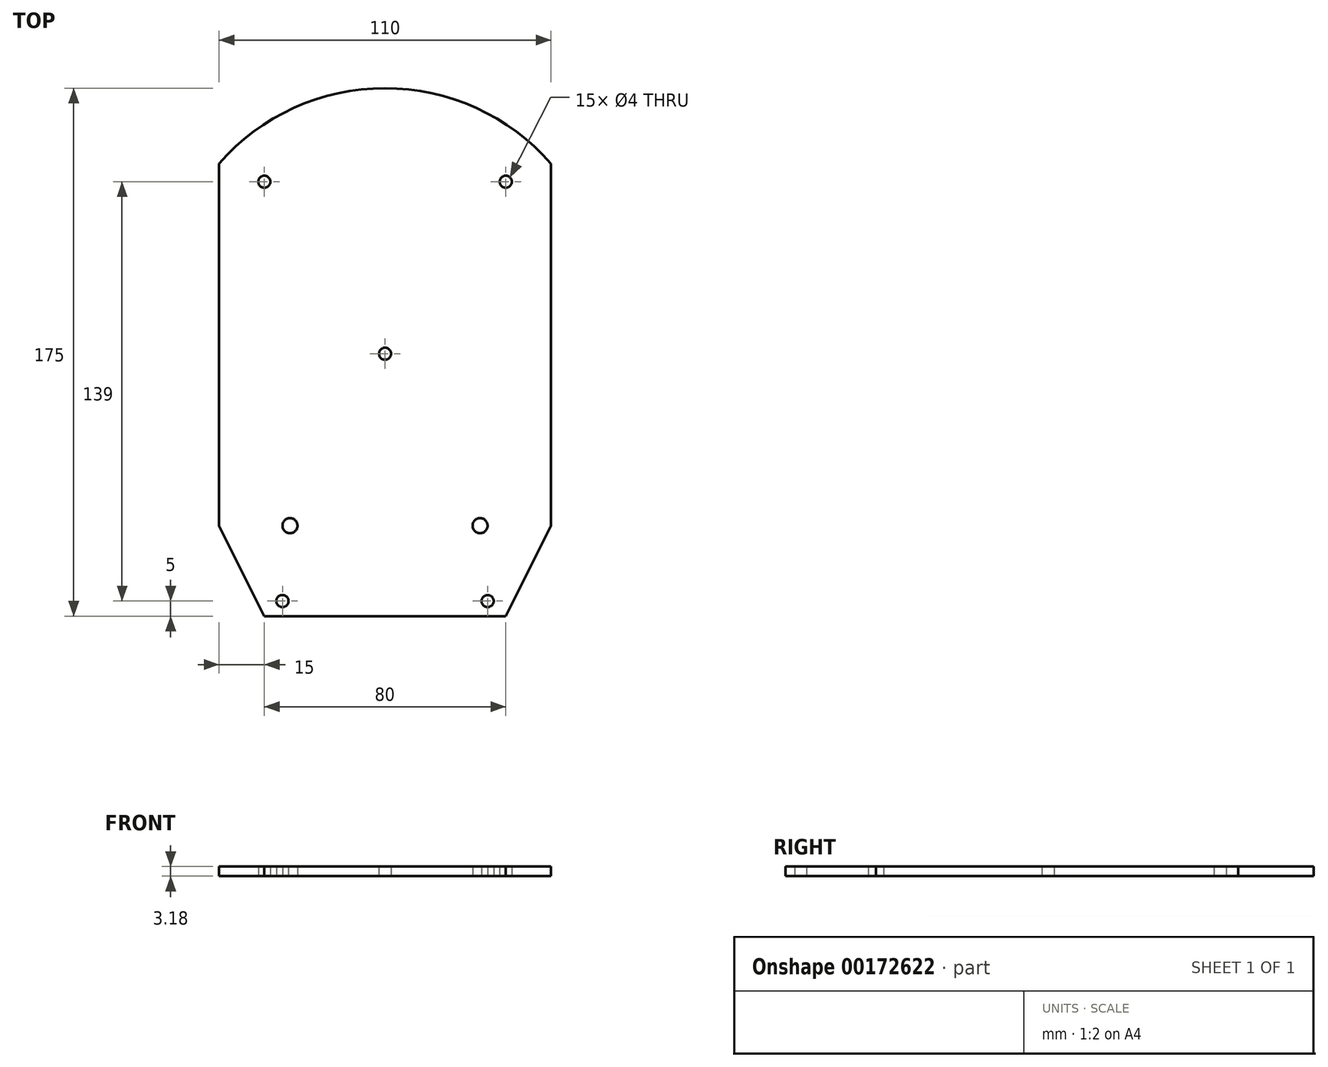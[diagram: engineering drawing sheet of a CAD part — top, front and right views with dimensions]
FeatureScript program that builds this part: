
annotation { "Feature Type Name" : "Feature", "Feature Type Description" : "" }
export const myFeature = defineFeature(function(context is Context, id is Id, definition is map)
    precondition{}
    {
        {
            var Q0;
            Q0=qCreatedBy(makeId("Top.planeOp"),FACE);
            var sketch = newSketch(context, id + "F0", { "sketchPlane" : qUnion([Q0])});
            skLineSegment(sketch, "E0.top", {"start": v(-40, -87.5) * mm, "end": v(40, -87.5) * mm});
            skLineSegment(sketch, "E0.left", {"start": v(-55, 62.5) * mm, "end": v(-55, -57.5) * mm});
            skLineSegment(sketch, "E0.right", {"start": v(55, 62.5) * mm, "end": v(55, -57.5) * mm});
            skPoint(sketch, "E0.middle", {"position": v(0, 0) * mm});
            skPoint(sketch, "E1", {"position": v(0, -87.5) * mm});
            skPoint(sketch, "E2", {"position": v(-40, -87.5) * mm});
            skPoint(sketch, "E3", {"position": v(40, -87.5) * mm});
            skLineSegment(sketch, "E4", {"start": v(-55, -57.5) * mm, "end": v(-40, -87.5) * mm});
            skLineSegment(sketch, "E5", {"start": v(55, -57.5) * mm, "end": v(40, -87.5) * mm});
            skPoint(sketch, "E6", {"position": v(0, 87.5) * mm});
            skArc(sketch, "E7", {"start": v(55, 62.5) * mm, "mid": v(0, 87.5) * mm, "end": v(-55, 62.5) * mm});
            skPoint(sketch, "E8", {"position": v(-34, -82.5) * mm});
            skCircle(sketch, "E9", {"center": v(-34, -82.5) * mm, "radius": 2 * mm});
            skPoint(sketch, "E10", {"position": v(-40, 56.5) * mm});
            skLineSegment(sketch, "E11", {"start": v(-55, 62.5) * mm, "end": v(-16.67, 62.5) * mm, "construction": true});
            skCircle(sketch, "E12", {"center": v(-40, 56.5) * mm, "radius": 2 * mm});
            skCircle(sketch, "E13.MirrorC", {"center": v(40, 56.5) * mm, "radius": 2 * mm});
            skCircle(sketch, "E14.MirrorC", {"center": v(34, -82.5) * mm, "radius": 2 * mm});
            skPoint(sketch, "E15", {"position": v(0, -0.5) * mm});
            skCircle(sketch, "E16", {"center": v(0, -0.5) * mm, "radius": 2 * mm});
            skLineSegment(sketch, "E17", {"start": v(-55, -57.5) * mm, "end": v(55, -57.5) * mm, "construction": true});
            skPoint(sketch, "E18", {"position": v(-31.5, -57.5) * mm});
            skCircle(sketch, "E19", {"center": v(-31.5, -57.5) * mm, "radius": 2.5 * mm});
            skCircle(sketch, "E20.MirrorC", {"center": v(31.5, -57.5) * mm, "radius": 2.5 * mm});
            skSolve(sketch);
        }
        {
            var Q0;
            Q0 = qSketchRegion(id + "F0", true);
            extrude(context, id + "F1", {"entities" : qUnion([Q0]), "depth" : 3.17 * mm});
        }
    });
